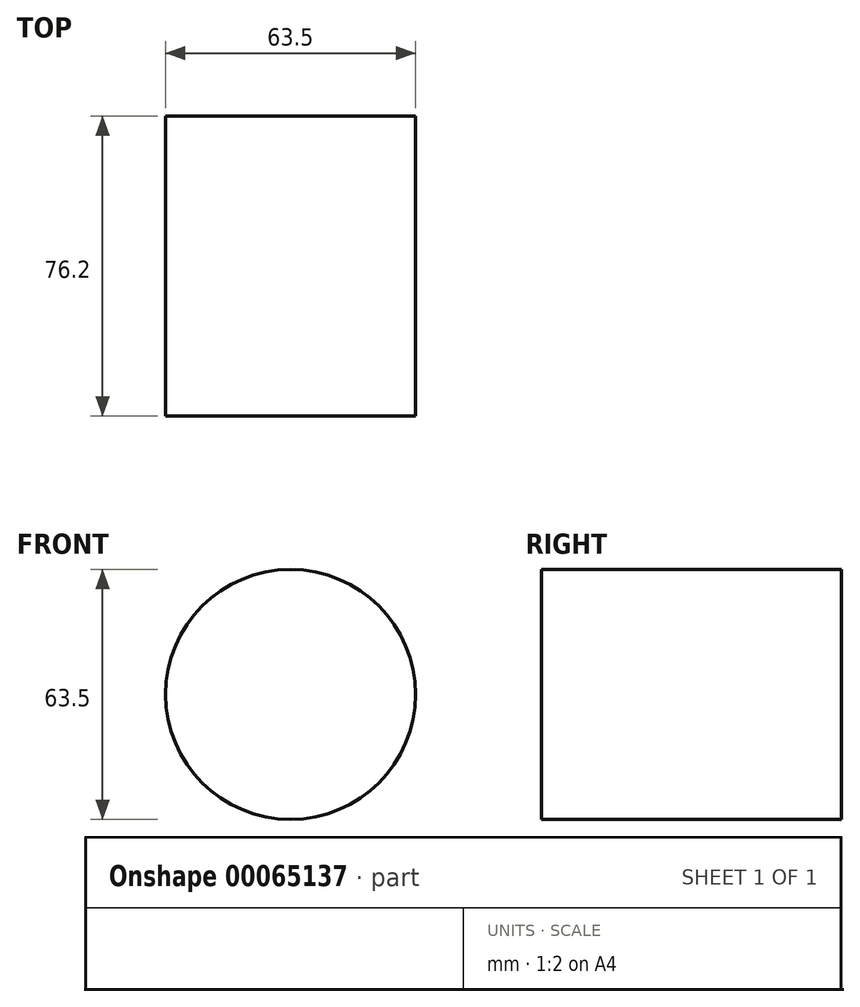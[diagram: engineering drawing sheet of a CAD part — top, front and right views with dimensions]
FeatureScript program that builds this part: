
annotation { "Feature Type Name" : "Feature", "Feature Type Description" : "" }
export const myFeature = defineFeature(function(context is Context, id is Id, definition is map)
    precondition{}
    {
        {
            var Q0;
            Q0=qCreatedBy(makeId("Front.planeOp"),FACE);
            var sketch = newSketch(context, id + "F0", { "sketchPlane" : qUnion([Q0])});
            skCircle(sketch, "E0", {"center": v(0, 0) * mm, "radius": 31.75 * mm});
            skSolve(sketch);
        }
        {
            var Q0;
            Q0=makeQuery(id+"F0.imprint","IMPRINT",FACE,{"disambiguationData":[TD([[makeQuery(id+"F0.imprint","IMPRINT",EDGE,{"derivedFrom":sQuery(id+"F0.wireOp",EDGE,"E0")}),1.0]])]});
            extrude(context, id + "F1", {"entities" : qUnion([Q0]), "oppositeDirection" : true, "depth" : 76.2 * mm});
        }
    });
